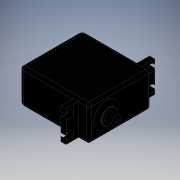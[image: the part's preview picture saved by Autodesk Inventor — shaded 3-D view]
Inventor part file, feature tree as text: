
AUTODESK INVENTOR PART (.ipt)
format: ipt  version: 2016 (Build 200138000, 138)  size: 268,800 bytes
history: native  units: in
note: dims shown in document units (in); Inventor stores cm internally (conversion verified against a paired STEP export)
features: extrude x9, sketch x9, fillet x4
ambient origin geometry x8: Origin, YZ Plane, XZ Plane, XY Plane, X Axis, Y Axis, Z Axis, Center Point
bodies: Solid1 (feature_tree)
feature tree (22):
  extrude  "Extrusion1"  Depth=0.787in
  extrude  "Extrusion2"  Depth=0.58in
  fillet  "Fillet1"  Radius=0.393in
  extrude  "Extrusion3"  Depth=0.058in TaperAngle=0.0deg
  extrude  "Extrusion4"  Depth=0.015in TaperAngle=0.0deg
  extrude  "Extrusion5"  Depth=0.16in TaperAngle=0.0deg
  fillet  "Fillet2"  Radius=0.08in
  fillet  "Fillet3"  Radius=0.16in
  fillet  "Fillet4"  Radius=0.1in
  sketch  "Sketch1"  dims[d0=1.594in d1=0.787in]
  sketch  "Sketch2"  dims[d2=1.421in d3=0.0in d4=0.58in d5=0.393in]
  sketch  "Sketch3"  dims[d6=0.409in d7=0.058in d8=0.0in]
  sketch  "Sketch4"  dims[d9=0.125in d11=0.015in d12=0.0in]
  sketch  "Sketch5"  dims[d13=0.23in d14=0.16in d15=0.0in d16=0.08in d17=0.16in d18=0.0in]
  extrude  "Extrusion9"  Depth=0.06in
  extrude  "Extrusion10"  [1 undecoded]
  extrude  "Extrusion11"  [1 undecoded]
  extrude  "Extrusion12"  [1 undecoded]
  sketch  "Sketch8"  dims[d19=0.118in d20=0.708in d21=1.145in d22=0.295in d23=0.0in d24=0.59in d25=0.177in d26=0.219in d27=0.177in d28=0.219in d37=0.295in d38=0.0in]
  sketch  "Sketch9"  dims[d39=1.145in d40=0.118in d41=0.708in d43=0.0in d44=0.295in]
  sketch  "Sketch10"  dims[d45=0.177in d46=0.59in d47=0.219in d48=0.177in d49=0.219in d51=0.0in d52=0.295in d53=0.1in]
  sketch  "Sketch11"  dims[d54=0.06in d55=0.06in d56=1.145in d57=0.118in d58=0.708in d60=0.0in d61=0.295in d62=0.219in d63=0.219in d64=0.177in d65=0.59in d66=0.177in d68=0.0in d69=0.295in]
note: 3 required parameter values undecoded (feature->parameter linkage not recoverable at this tier; creation-order binding heuristic only, values carry confidence <= 0.55)
